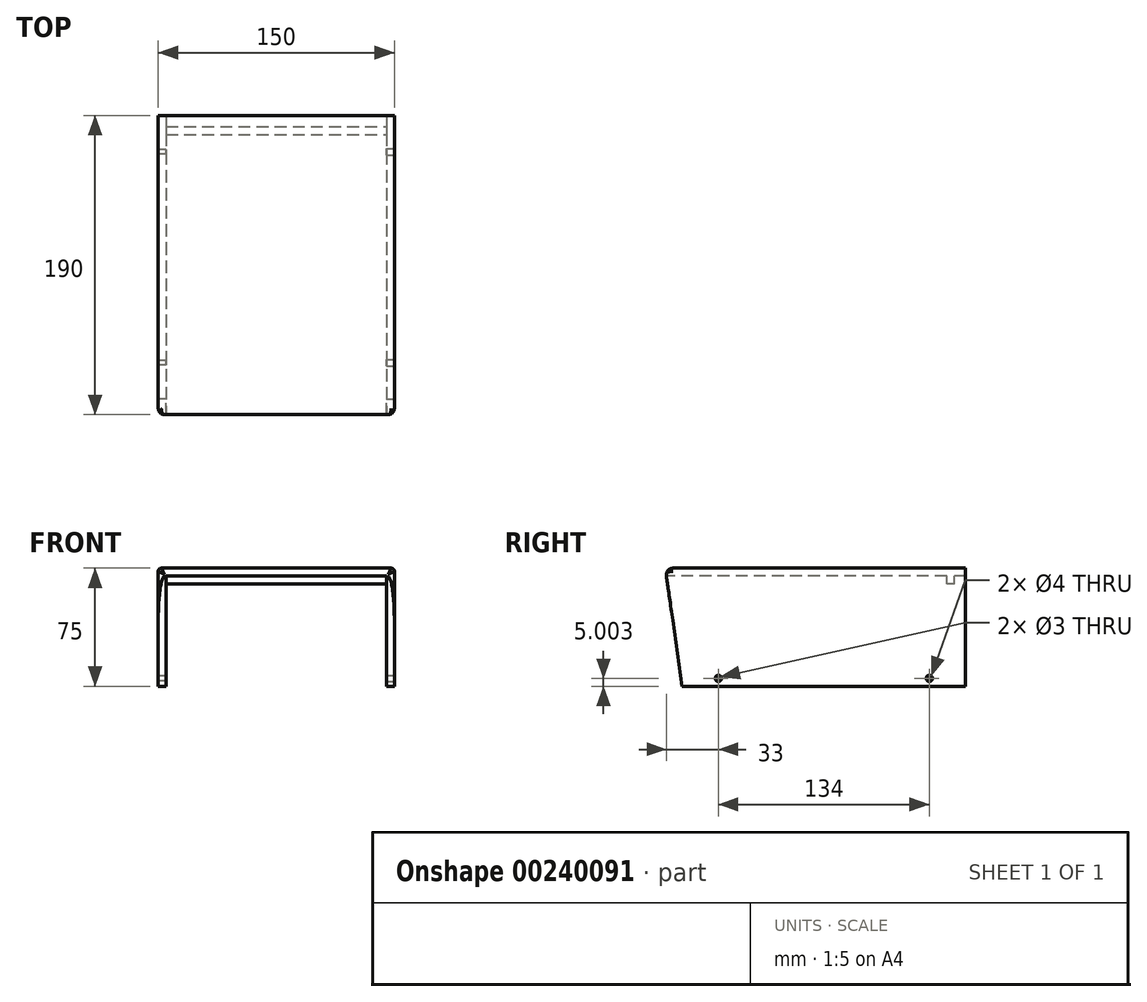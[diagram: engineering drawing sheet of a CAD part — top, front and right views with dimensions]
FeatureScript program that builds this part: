
annotation { "Feature Type Name" : "Feature", "Feature Type Description" : "" }
export const myFeature = defineFeature(function(context is Context, id is Id, definition is map)
    precondition{}
    {
        {
            var Q0;
            Q0=qCreatedBy(makeId("Front.planeOp"),FACE);
            var sketch = newSketch(context, id + "F0", { "sketchPlane" : qUnion([Q0])});
            skLineSegment(sketch, "E0", {"start": v(-75.84, 40.7) * mm, "end": v(74.16, 40.7) * mm});
            skLineSegment(sketch, "E1", {"start": v(74.16, 40.7) * mm, "end": v(74.16, -34.3) * mm});
            skLineSegment(sketch, "E2", {"start": v(74.16, -34.3) * mm, "end": v(69.16, -34.3) * mm});
            skLineSegment(sketch, "E3", {"start": v(69.16, -34.3) * mm, "end": v(69.16, 35.7) * mm});
            skLineSegment(sketch, "E4", {"start": v(69.16, 35.7) * mm, "end": v(-70.84, 35.7) * mm});
            skLineSegment(sketch, "E5", {"start": v(-70.84, 35.7) * mm, "end": v(-70.84, -34.3) * mm});
            skLineSegment(sketch, "E6", {"start": v(-70.84, -34.3) * mm, "end": v(-75.84, -34.3) * mm});
            skLineSegment(sketch, "E7", {"start": v(-75.84, -34.3) * mm, "end": v(-75.84, 40.7) * mm});
            skSolve(sketch);
        }
        {
            var Q0;
            Q0=makeQuery(id+"F0.imprint","IMPRINT",FACE,{"disambiguationData":[TD([[makeQuery(id+"F0.imprint","IMPRINT",EDGE,{"derivedFrom":sQuery(id+"F0.wireOp",EDGE,"E0")}),-1.0]])]});
            extrude(context, id + "F1", {"entities" : qUnion([Q0]), "oppositeDirection" : true, "depth" : 190 * mm});
        }
        {
            var Q0;
            Q0=makeQuery(id+"F1.opExtrude","SWEPT_FACE",FACE,{"disambiguationData":[OSD([sQuery(id+"F0.wireOp",EDGE,"E7")])]});
            var sketch = newSketch(context, id + "F2", { "sketchPlane" : qUnion([Q0])});
            skLineSegment(sketch, "E8", {"start": v(0, 35.54) * mm, "end": v(-10, -34.3) * mm});
            skLineSegment(sketch, "E9", {"start": v(-10, -34.3) * mm, "end": v(0, -34.3) * mm});
            skLineSegment(sketch, "E10", {"start": v(0, -34.3) * mm, "end": v(0, 35.54) * mm});
            skSolve(sketch);
        }
        {
            var Q0;
            Q0=makeQuery(id+"F2.imprint","IMPRINT",FACE,{"disambiguationData":[TD([[makeQuery(id+"F2.imprint","IMPRINT",EDGE,{"derivedFrom":sQuery(id+"F2.wireOp",EDGE,"E8")}),1.0]])]});
            extrude(context, id + "F3", {"entities" : qUnion([Q0]), "operationType" : NewBodyOperationType.REMOVE, "oppositeDirection" : true, "depth" : 25 * mm});
        }
        {
            var Q0;
            Q0=makeQuery(id+"F1.opExtrude","SWEPT_FACE",FACE,{"disambiguationData":[OSD([sQuery(id+"F0.wireOp",EDGE,"E1")])]});
            var sketch = newSketch(context, id + "F4", { "sketchPlane" : qUnion([Q0])});
            skLineSegment(sketch, "E11", {"start": v(0, 35.25) * mm, "end": v(10, -34.3) * mm});
            skLineSegment(sketch, "E12", {"start": v(10, -34.3) * mm, "end": v(0, -34.3) * mm});
            skLineSegment(sketch, "E13", {"start": v(0, -34.3) * mm, "end": v(0, 35.25) * mm});
            skSolve(sketch);
        }
        {
            var Q0;
            Q0=makeQuery(id+"F4.imprint","IMPRINT",FACE,{"disambiguationData":[TD([[makeQuery(id+"F4.imprint","IMPRINT",EDGE,{"derivedFrom":sQuery(id+"F4.wireOp",EDGE,"E11")}),-1.0]])]});
            extrude(context, id + "F5", {"entities" : qUnion([Q0]), "operationType" : NewBodyOperationType.REMOVE, "oppositeDirection" : true, "depth" : 25 * mm});
        }
        {
            var Q0;
            Q0=makeQuery(id+"F1.opExtrude","SWEPT_FACE",FACE,{"disambiguationData":[OSD([sQuery(id+"F0.wireOp",EDGE,"E1")])]});
            var sketch = newSketch(context, id + "F6", { "sketchPlane" : qUnion([Q0])});
            skCircle(sketch, "E14", {"center": v(167, -29.3) * mm, "radius": 2 * mm});
            skCircle(sketch, "E15", {"center": v(33, -29.3) * mm, "radius": 2 * mm});
            skSolve(sketch);
        }
        {
            var Q0;
            Q0=makeQuery(id+"F6.imprint","IMPRINT",FACE,{"disambiguationData":[TD([[makeQuery(id+"F6.imprint","IMPRINT",EDGE,{"derivedFrom":sQuery(id+"F6.wireOp",EDGE,"E15")}),1.0]])]});
            var Q1;
            Q1=makeQuery(id+"F6.imprint","IMPRINT",FACE,{"disambiguationData":[TD([[makeQuery(id+"F6.imprint","IMPRINT",EDGE,{"derivedFrom":sQuery(id+"F6.wireOp",EDGE,"E14")}),1.0]])]});
            extrude(context, id + "F7", {"entities" : qUnion([Q0, Q1]), "operationType" : NewBodyOperationType.REMOVE, "oppositeDirection" : true, "depth" : 25 * mm});
        }
        {
            var Q0;
            Q0=makeQuery(id+"F1.opExtrude","SWEPT_FACE",FACE,{"disambiguationData":[OSD([sQuery(id+"F0.wireOp",EDGE,"E7")])]});
            var sketch = newSketch(context, id + "F8", { "sketchPlane" : qUnion([Q0])});
            skCircle(sketch, "E16", {"center": v(-167, -29.3) * mm, "radius": 1.5 * mm});
            skCircle(sketch, "E17", {"center": v(-33, -29.3) * mm, "radius": 1.5 * mm});
            skSolve(sketch);
        }
        {
            var Q0;
            Q0=makeQuery(id+"F8.imprint","IMPRINT",FACE,{"disambiguationData":[TD([[makeQuery(id+"F8.imprint","IMPRINT",EDGE,{"derivedFrom":sQuery(id+"F8.wireOp",EDGE,"E16")}),1.0]])]});
            var Q1;
            Q1=makeQuery(id+"F8.imprint","IMPRINT",FACE,{"disambiguationData":[TD([[makeQuery(id+"F8.imprint","IMPRINT",EDGE,{"derivedFrom":sQuery(id+"F8.wireOp",EDGE,"E17")}),1.0]])]});
            extrude(context, id + "F9", {"entities" : qUnion([Q0, Q1]), "operationType" : NewBodyOperationType.REMOVE, "oppositeDirection" : true, "depth" : 25 * mm});
        }
        {
            var Q0;
            Q0=makeQuery(id+"F3.boolean.opBoolean","COPY",EDGE,{"derivedFrom":makeQuery(id+"F3.opExtrude","CAP_EDGE",EDGE,{"disambiguationData":[OSD([sQuery(id+"F2.wireOp",EDGE,"E8")])],"isStart":true})});
            var Q1;
            Q1=makeQuery(id+"F1.opExtrude","CAP_EDGE",EDGE,{"disambiguationData":[OSD([sQuery(id+"F0.wireOp",EDGE,"E7")])],"isStart":true});
            var Q2;
            Q2=makeQuery(id+"F1.opExtrude","CAP_EDGE",EDGE,{"disambiguationData":[OSD([sQuery(id+"F0.wireOp",EDGE,"E0")])],"isStart":true});
            var Q3;
            Q3=makeQuery(id+"F5.boolean.opBoolean","COPY",EDGE,{"derivedFrom":makeQuery(id+"F5.opExtrude","CAP_EDGE",EDGE,{"disambiguationData":[OSD([sQuery(id+"F4.wireOp",EDGE,"E11")])],"isStart":true})});
            var Q4;
            Q4=makeQuery(id+"F1.opExtrude","CAP_EDGE",EDGE,{"disambiguationData":[OSD([sQuery(id+"F0.wireOp",EDGE,"E1")])],"isStart":true});
            fillet(context, id + "F10", {"entities" : qUnion([Q0, Q1, Q2, Q3, Q4]), "radius" : 4 * mm, "tangentPropagation" : true, "allowEdgeOverflow" : false});
        }
        {
            var Q0;
            Q0=makeQuery(id+"F1.opExtrude","SWEPT_EDGE",EDGE,{"disambiguationData":[OSD([sQuery(id+"F0.wireOp",EDGE,"E0"),sQuery(id+"F0.wireOp",EDGE,"E1")])]});
            var Q1;
            Q1=makeQuery(id+"F1.opExtrude","SWEPT_EDGE",EDGE,{"disambiguationData":[OSD([sQuery(id+"F0.wireOp",EDGE,"E0"),sQuery(id+"F0.wireOp",EDGE,"E7")])]});
            fillet(context, id + "F11", {"entities" : qUnion([Q0, Q1]), "radius" : 2 * mm, "tangentPropagation" : true, "allowEdgeOverflow" : false});
        }
        {
            var Q0;
            Q0=makeQuery(id+"F1.opExtrude","SWEPT_FACE",FACE,{"disambiguationData":[OSD([sQuery(id+"F0.wireOp",EDGE,"E4")])]});
            var sketch = newSketch(context, id + "F12", { "sketchPlane" : qUnion([Q0])});
            skLineSegment(sketch, "E18.bottom", {"start": v(-70.84, -178) * mm, "end": v(69.16, -178) * mm});
            skLineSegment(sketch, "E18.top", {"start": v(-70.84, -183) * mm, "end": v(69.16, -183) * mm});
            skLineSegment(sketch, "E18.left", {"start": v(-70.84, -178) * mm, "end": v(-70.84, -183) * mm});
            skLineSegment(sketch, "E18.right", {"start": v(69.16, -178) * mm, "end": v(69.16, -183) * mm});
            skSolve(sketch);
        }
        {
            var Q0;
            Q0=makeQuery(id+"F12.imprint","IMPRINT",FACE,{"disambiguationData":[TD([[makeQuery(id+"F12.imprint","IMPRINT",EDGE,{"derivedFrom":sQuery(id+"F12.wireOp",EDGE,"E18.bottom")}),-1.0]])]});
            extrude(context, id + "F13", {"entities" : qUnion([Q0]), "operationType" : NewBodyOperationType.ADD, "depth" : 5 * mm});
        }
    });
